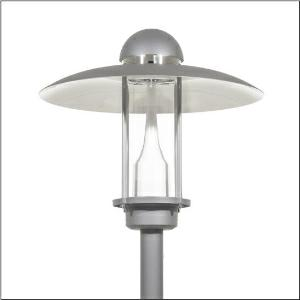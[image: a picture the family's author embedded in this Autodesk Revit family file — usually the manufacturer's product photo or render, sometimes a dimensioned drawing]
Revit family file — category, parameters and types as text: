
# Revit family: city-light_elegance_iq___st1_2a_5xa5265kf14h_1fe5
name_source: partatom
category: Lighting Fixtures
units: mm (PartAtom-declared; Revit-internal decimal feet)

## family parameters
Cut with Voids When Loaded = No
Host = Face
Light Source = No
Part Type = Normal
Room Calculation Point = No
Round Connector Dimension = Use Diameter
Shared = No

## types (1)
- --- (1 x LED, 1470 lm, 10 W, 4000K)
    Apparent Load = 10 VA
    CIE Flux Codes = 22 62 94 98 100
    Color Rendering = 70
    Color Temperature = 4000K
    Default Elevation = 1800 mm
    Description = City-Light Elegance iQ, mast luminaire, Module 540 iQ-SR, primary light control with 3 zone facetted reflector, of plastic, silver coated, highly specular, structured, primary optical cover: cover, of PMMA, transparent, light distribution: ST1.2a, light emission: direct distribution, primary light characteristic: asymmetric, installation type: post-top, LED, High Power LED, rated luminous flux: 1.470lm, luminous efficacy: 147lm/W, light colour: 740, colour temperature: 4000K, control gear: ECG iQ, control: presetting dimming logarithmic, Street-Remote, Auto-Match, Temp-Guard, Lumen-Switch, Night-Set, Smart-Wire, Light-Fading, Desk-Remote (wireless, voltage-free reading and setting of iQ features in the workshop via application-optimized NFC function/RFID function), optimised constant luminous flux control (CLO 2.0), with terminal, 6-pole, max. 2.5mm², mains connection: 230..240V, AC, 50/60Hz, start of lifetime: 10W, end of service life: 10W, reduction: 5W, luminaire housing, upper part, of aluminium, coated, Siteco® metallic grey (DB 702S), diameter: 750mm, height: 675mm, spigot size: d x l = 76 x 70mm (post-top) | with reducer (optional accessory) 60 x 70mm, post-top mast mounting element, of diecast aluminium, coated, Siteco® metallic grey (DB 702S), Module 540 iQ-SR, traffic white (RAL 9016), equipment: standard, protection rating (complete): IP65, insulation class (complete): insulation class II (safety insulation), certification: CE, ENEC, VDE, packaging unit: 1 piece

Light Distribution: ST1.2a
    Height = 675 mm
    Lamp = 1 x LED
    Lamp Light Flux = 1470 lm
    Lamp Power = 10 W
    Lamp count = 1
    Length = 750 mm
    Luminous efficacy = 147 lm/W
    Manufacturer = Siteco
    ModVariant = No
    Model = 5XA5265KF14H
    Number of Poles = 1
    OnlyDefault = Yes
    Power Factor = 1
    Product Name = City-Light Elegance iQ | ST1.2a
    Product group = mast luminaire | pylon top
    ProductGroupID = 6100
    Protection Class = Protection class II
    Protection Degree = IP 65
    RLX_Detail_Level = 1
    RLX_Emergency_Light_Flux = 0 lm
    RLX_Emergency_Type = 0
    RLX_Emergency_Type_DB = No
    RlxData = <blob elided: 104113 chars, md5=e086857c>
    Socket = socket
    Standby Power = 0 W
    System Light Flux = 1470 lm
    System Power = 10 W
    Type Comments = factory setting: luminous flux: 100 % | dim-lin: 254 | 401 mA
    Type Image = l_1006912.jpg
    URL = http://relux.com
    VarID = @adj_092147
    Voltage = 0 V
    Weight = 0.00 kg
    Width = 0 mm  [stored 0 ft]

note: [stored X ft] marks values corroborated as IEEE doubles in the binary element streams (Revit-internal decimal feet)

## geometry (parser evidence)
native form markers: Blend x4, Sweep x8
no freeform markers — native parametric forms only
